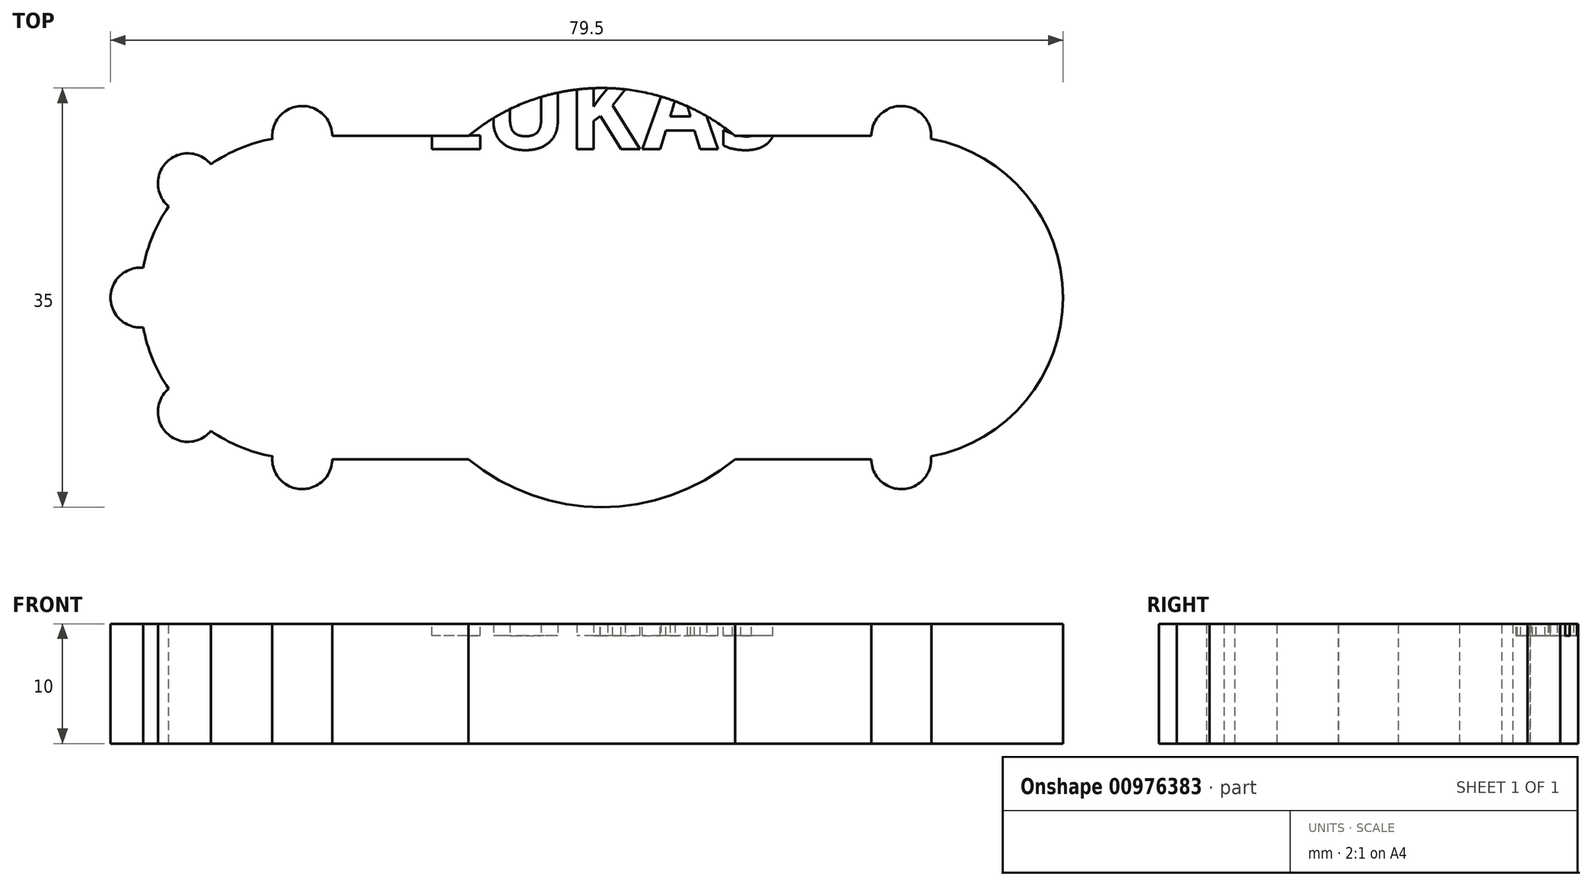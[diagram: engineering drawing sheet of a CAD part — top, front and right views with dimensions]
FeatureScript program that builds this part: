
annotation { "Feature Type Name" : "Feature", "Feature Type Description" : "" }
export const myFeature = defineFeature(function(context is Context, id is Id, definition is map)
    precondition{}
    {
        {
            var Q0;
            Q0=qCreatedBy(makeId("Top.planeOp"),FACE);
            var sketch = newSketch(context, id + "F0", { "sketchPlane" : qUnion([Q0])});
            skLineSegment(sketch, "E0.bottom", {"start": v(25, 13.5) * mm, "end": v(-25, 13.5) * mm});
            skLineSegment(sketch, "E0.top", {"start": v(25, -13.5) * mm, "end": v(-25, -13.5) * mm});
            skLineSegment(sketch, "E0.left", {"start": v(25, 13.5) * mm, "end": v(25, -13.5) * mm});
            skLineSegment(sketch, "E0.right", {"start": v(-25, 13.5) * mm, "end": v(-25, -13.5) * mm});
            skPoint(sketch, "E0.middle", {"position": v(0, 0) * mm});
            skCircle(sketch, "E1", {"center": v(-25, 0) * mm, "radius": 13.5 * mm});
            skCircle(sketch, "E2", {"center": v(25, 0) * mm, "radius": 13.5 * mm});
            skCircle(sketch, "E3", {"center": v(0, 0) * mm, "radius": 11.05 * mm});
            skCircle(sketch, "E4.cCircle", {"center": v(-25, 0) * mm, "radius": 8.55 * mm, "construction": true});
            skLineSegment(sketch, "E4.0", {"start": v(-25, 9.87) * mm, "end": v(-16.45, 4.94) * mm});
            skLineSegment(sketch, "E4.1", {"start": v(-16.45, 4.94) * mm, "end": v(-16.45, -4.94) * mm});
            skLineSegment(sketch, "E4.2", {"start": v(-16.45, -4.94) * mm, "end": v(-25, -9.87) * mm});
            skLineSegment(sketch, "E4.3", {"start": v(-25, -9.87) * mm, "end": v(-33.55, -4.94) * mm});
            skLineSegment(sketch, "E4.4", {"start": v(-33.55, -4.94) * mm, "end": v(-33.55, 4.94) * mm});
            skLineSegment(sketch, "E4.5", {"start": v(-33.55, 4.94) * mm, "end": v(-25, 9.87) * mm});
            skPoint(sketch, "E4.0.midPoint", {"position": v(-20.73, 7.4) * mm});
            skCircle(sketch, "E5.cCircle", {"center": v(25, 0) * mm, "radius": 8.55 * mm, "construction": true});
            skLineSegment(sketch, "E5.0", {"start": v(25, 9.87) * mm, "end": v(33.55, 4.94) * mm});
            skLineSegment(sketch, "E5.1", {"start": v(33.55, 4.94) * mm, "end": v(33.55, -4.94) * mm});
            skLineSegment(sketch, "E5.2", {"start": v(33.55, -4.94) * mm, "end": v(25, -9.87) * mm});
            skLineSegment(sketch, "E5.3", {"start": v(25, -9.87) * mm, "end": v(16.45, -4.94) * mm});
            skLineSegment(sketch, "E5.4", {"start": v(16.45, -4.94) * mm, "end": v(16.45, 4.94) * mm});
            skLineSegment(sketch, "E5.5", {"start": v(16.45, 4.94) * mm, "end": v(25, 9.87) * mm});
            skPoint(sketch, "E5.0.midPoint", {"position": v(29.27, 7.4) * mm});
            skArc(sketch, "E6", {"start": v(-14.98, 9.05) * mm, "mid": v(-17.5, 0) * mm, "end": v(-14.98, -9.05) * mm, "construction": true});
            skArc(sketch, "E7.trimOffspring", {"start": v(11.14, 13.5) * mm, "mid": v(0, 17.5) * mm, "end": v(-11.14, 13.5) * mm});
            skArc(sketch, "E8.trimOffspring", {"start": v(14.98, -9.05) * mm, "mid": v(17.5, 0) * mm, "end": v(14.98, 9.05) * mm, "construction": true});
            skArc(sketch, "E9.trimOffspring", {"start": v(-11.14, -13.5) * mm, "mid": v(0, -17.5) * mm, "end": v(11.14, -13.5) * mm});
            skSolve(sketch);
        }
        {
            var Q0;
            Q0 = qSketchRegion(id + "F0", true);
            extrude(context, id + "F1", {"entities" : qUnion([Q0]), "endBound" : BoundingType.SYMMETRIC, "depth" : 10 * mm, "offsetDistance" : 25.4 * mm});
        }
        {
            var Q0;
            Q0=qCreatedBy(makeId("Top.planeOp"),FACE);
            var sketch = newSketch(context, id + "F2", { "sketchPlane" : qUnion([Q0])});
            skArc(sketch, "E10.0", {"start": v(-25, 13.5) * mm, "mid": v(-38.5, 0) * mm, "end": v(-25, -13.5) * mm});
            skLineSegment(sketch, "E11.0", {"start": v(25, 13.5) * mm, "end": v(-25, 13.5) * mm});
            skArc(sketch, "E12.0", {"start": v(25, -13.5) * mm, "mid": v(38.5, 0) * mm, "end": v(25, 13.5) * mm});
            skLineSegment(sketch, "E13.0", {"start": v(25, -13.5) * mm, "end": v(-25, -13.5) * mm});
            skCircle(sketch, "E14", {"center": v(-25, 13.5) * mm, "radius": 2.5 * mm});
            skCircle(sketch, "E15.1.0", {"center": v(-34.55, 9.55) * mm, "radius": 2.5 * mm});
            skCircle(sketch, "E15.2.0", {"center": v(-38.5, 0) * mm, "radius": 2.5 * mm});
            skCircle(sketch, "E15.3.0", {"center": v(-34.55, -9.55) * mm, "radius": 2.5 * mm});
            skCircle(sketch, "E15.4.0", {"center": v(-25, -13.5) * mm, "radius": 2.5 * mm});
            skLineSegment(sketch, "E15.anchor1", {"start": v(-25, 0) * mm, "end": v(-25, 13.5) * mm, "construction": true});
            skLineSegment(sketch, "E15.anchor2", {"start": v(-25, 0) * mm, "end": v(-25, -13.5) * mm, "construction": true});
            skLineSegment(sketch, "E16.MirrorCS", {"start": v(25, 0) * mm, "end": v(25, -13.5) * mm, "construction": true});
            skLineSegment(sketch, "E17.MirrorCS", {"start": v(25, 0) * mm, "end": v(25, 13.5) * mm, "construction": true});
            skCircle(sketch, "E18.MirrorC", {"center": v(25, -13.5) * mm, "radius": 2.5 * mm});
            skCircle(sketch, "E19.MirrorC", {"center": v(34.55, -9.55) * mm, "radius": 2.5 * mm});
            skCircle(sketch, "E20.MirrorC", {"center": v(38.5, 0) * mm, "radius": 2.5 * mm});
            skArc(sketch, "E21.MirrorCS", {"start": v(25, 13.5) * mm, "mid": v(38.5, 0) * mm, "end": v(25, -13.5) * mm});
            skCircle(sketch, "E22.MirrorC", {"center": v(34.55, 9.55) * mm, "radius": 2.5 * mm});
            skCircle(sketch, "E23.MirrorC", {"center": v(25, 13.5) * mm, "radius": 2.5 * mm});
            skSolve(sketch);
        }
        {
            var Q0;
            {var subQ0=sQuery(id+"F2.wireOp",EDGE,"E11.0");var subQ1=sQuery(id+"F2.wireOp",EDGE,"E10.0");var subQ2=makeQuery(id+"F2.imprint","INTERSECT",VERTEX,{"derivedFrom":[subQ1,subQ0]});Q0=makeQuery(id+"F2.imprint","IMPRINT",FACE,{"disambiguationData":[TD([[makeQuery(id+"F2.imprint","IMPRINT",EDGE,{"disambiguationData":[TD([[subQ2,-1.0]])],"derivedFrom":subQ1}),-1.0]])]});}
            var Q1;
            {var subQ0=sQuery(id+"F2.wireOp",EDGE,"E15.1.0");var subQ1=sQuery(id+"F2.wireOp",EDGE,"E10.0");var subQ2=makeQuery(id+"F2.imprint","INTERSECT",VERTEX,{"disambiguationData":[OD(0.0)],"derivedFrom":[subQ1,subQ0]});Q1=makeQuery(id+"F2.imprint","IMPRINT",FACE,{"disambiguationData":[TD([[makeQuery(id+"F2.imprint","IMPRINT",EDGE,{"disambiguationData":[TD([[subQ2,-1.0]])],"derivedFrom":subQ1}),-1.0]])]});}
            var Q2;
            {var subQ0=sQuery(id+"F2.wireOp",EDGE,"E15.2.0");var subQ1=sQuery(id+"F2.wireOp",EDGE,"E10.0");var subQ2=makeQuery(id+"F2.imprint","INTERSECT",VERTEX,{"disambiguationData":[OD(0.0)],"derivedFrom":[subQ1,subQ0]});Q2=makeQuery(id+"F2.imprint","IMPRINT",FACE,{"disambiguationData":[TD([[makeQuery(id+"F2.imprint","IMPRINT",EDGE,{"disambiguationData":[TD([[subQ2,-1.0]])],"derivedFrom":subQ1}),-1.0]])]});}
            var Q3;
            {var subQ0=sQuery(id+"F2.wireOp",EDGE,"E15.3.0");var subQ1=sQuery(id+"F2.wireOp",EDGE,"E10.0");var subQ2=makeQuery(id+"F2.imprint","INTERSECT",VERTEX,{"disambiguationData":[OD(0.0)],"derivedFrom":[subQ1,subQ0]});Q3=makeQuery(id+"F2.imprint","IMPRINT",FACE,{"disambiguationData":[TD([[makeQuery(id+"F2.imprint","IMPRINT",EDGE,{"disambiguationData":[TD([[subQ2,-1.0]])],"derivedFrom":subQ1}),-1.0]])]});}
            var Q4;
            {var subQ0=sQuery(id+"F2.wireOp",EDGE,"E13.0");var subQ1=sQuery(id+"F2.wireOp",EDGE,"E10.0");var subQ2=makeQuery(id+"F2.imprint","INTERSECT",VERTEX,{"derivedFrom":[subQ1,subQ0]});Q4=makeQuery(id+"F2.imprint","IMPRINT",FACE,{"disambiguationData":[TD([[makeQuery(id+"F2.imprint","IMPRINT",EDGE,{"disambiguationData":[TD([[subQ2,1.0]])],"derivedFrom":subQ1}),-1.0]])]});}
            var Q5;
            {var subQ0=sQuery(id+"F2.wireOp",EDGE,"E21.MirrorCS");var subQ1=sQuery(id+"F2.wireOp",EDGE,"E11.0");var subQ2=makeQuery(id+"F2.imprint","INTERSECT",VERTEX,{"derivedFrom":[subQ1,subQ0]});Q5=makeQuery(id+"F2.imprint","IMPRINT",FACE,{"disambiguationData":[TD([[makeQuery(id+"F2.imprint","IMPRINT",EDGE,{"disambiguationData":[TD([[subQ2,-1.0]])],"derivedFrom":subQ1}),-1.0]])]});}
            var Q6;
            {var subQ0=sQuery(id+"F2.wireOp",EDGE,"E21.MirrorCS");var subQ1=sQuery(id+"F2.wireOp",EDGE,"E13.0");var subQ2=makeQuery(id+"F2.imprint","INTERSECT",VERTEX,{"derivedFrom":[subQ1,subQ0]});Q6=makeQuery(id+"F2.imprint","IMPRINT",FACE,{"disambiguationData":[TD([[makeQuery(id+"F2.imprint","IMPRINT",EDGE,{"disambiguationData":[TD([[subQ2,-1.0]])],"derivedFrom":subQ1}),1.0]])]});}
            var Q7;
            {var subQ0=sQuery(id+"F2.wireOp",EDGE,"E21.MirrorCS");var subQ1=sQuery(id+"F2.wireOp",EDGE,"E19.MirrorC");var subQ2=makeQuery(id+"F2.imprint","INTERSECT",VERTEX,{"disambiguationData":[OD(0.0)],"derivedFrom":[subQ1,subQ0]});Q7=makeQuery(id+"F2.imprint","IMPRINT",FACE,{"disambiguationData":[TD([[makeQuery(id+"F2.imprint","IMPRINT",EDGE,{"disambiguationData":[TD([[subQ2,-1.0]])],"derivedFrom":subQ1}),-1.0]])]});}
            var Q8;
            {var subQ0=sQuery(id+"F2.wireOp",EDGE,"E21.MirrorCS");var subQ1=sQuery(id+"F2.wireOp",EDGE,"E20.MirrorC");var subQ2=makeQuery(id+"F2.imprint","INTERSECT",VERTEX,{"disambiguationData":[OD(0.0)],"derivedFrom":[subQ1,subQ0]});Q8=makeQuery(id+"F2.imprint","IMPRINT",FACE,{"disambiguationData":[TD([[makeQuery(id+"F2.imprint","IMPRINT",EDGE,{"disambiguationData":[TD([[subQ2,-1.0]])],"derivedFrom":subQ1}),-1.0]])]});}
            var Q9;
            {var subQ0=sQuery(id+"F2.wireOp",EDGE,"E22.MirrorC");var subQ1=sQuery(id+"F2.wireOp",EDGE,"E21.MirrorCS");var subQ2=makeQuery(id+"F2.imprint","INTERSECT",VERTEX,{"disambiguationData":[OD(0.0)],"derivedFrom":[subQ1,subQ0]});Q9=makeQuery(id+"F2.imprint","IMPRINT",FACE,{"disambiguationData":[TD([[makeQuery(id+"F2.imprint","IMPRINT",EDGE,{"disambiguationData":[TD([[subQ2,-1.0]])],"derivedFrom":subQ1}),1.0]])]});}
            var Q10;
            {var subQ0=sQuery(id+"F2.wireOp",EDGE,"E11.0");var subQ1=sQuery(id+"F2.wireOp",EDGE,"E10.0");var subQ2=makeQuery(id+"F2.imprint","INTERSECT",VERTEX,{"derivedFrom":[subQ1,subQ0]});Q10=makeQuery(id+"F2.imprint","IMPRINT",FACE,{"disambiguationData":[TD([[makeQuery(id+"F2.imprint","IMPRINT",EDGE,{"disambiguationData":[TD([[subQ2,-1.0]])],"derivedFrom":subQ1}),1.0]])]});}
            var Q11;
            {var subQ0=sQuery(id+"F2.wireOp",EDGE,"E15.1.0");var subQ1=sQuery(id+"F2.wireOp",EDGE,"E10.0");var subQ2=makeQuery(id+"F2.imprint","INTERSECT",VERTEX,{"disambiguationData":[OD(0.0)],"derivedFrom":[subQ1,subQ0]});Q11=makeQuery(id+"F2.imprint","IMPRINT",FACE,{"disambiguationData":[TD([[makeQuery(id+"F2.imprint","IMPRINT",EDGE,{"disambiguationData":[TD([[subQ2,-1.0]])],"derivedFrom":subQ1}),1.0]])]});}
            var Q12;
            {var subQ0=sQuery(id+"F2.wireOp",EDGE,"E15.2.0");var subQ1=sQuery(id+"F2.wireOp",EDGE,"E10.0");var subQ2=makeQuery(id+"F2.imprint","INTERSECT",VERTEX,{"disambiguationData":[OD(0.0)],"derivedFrom":[subQ1,subQ0]});Q12=makeQuery(id+"F2.imprint","IMPRINT",FACE,{"disambiguationData":[TD([[makeQuery(id+"F2.imprint","IMPRINT",EDGE,{"disambiguationData":[TD([[subQ2,-1.0]])],"derivedFrom":subQ1}),1.0]])]});}
            var Q13;
            {var subQ0=sQuery(id+"F2.wireOp",EDGE,"E15.3.0");var subQ1=sQuery(id+"F2.wireOp",EDGE,"E10.0");var subQ2=makeQuery(id+"F2.imprint","INTERSECT",VERTEX,{"disambiguationData":[OD(0.0)],"derivedFrom":[subQ1,subQ0]});Q13=makeQuery(id+"F2.imprint","IMPRINT",FACE,{"disambiguationData":[TD([[makeQuery(id+"F2.imprint","IMPRINT",EDGE,{"disambiguationData":[TD([[subQ2,-1.0]])],"derivedFrom":subQ1}),1.0]])]});}
            var Q14;
            {var subQ0=sQuery(id+"F2.wireOp",EDGE,"E13.0");var subQ1=sQuery(id+"F2.wireOp",EDGE,"E10.0");var subQ2=makeQuery(id+"F2.imprint","INTERSECT",VERTEX,{"derivedFrom":[subQ1,subQ0]});Q14=makeQuery(id+"F2.imprint","IMPRINT",FACE,{"disambiguationData":[TD([[makeQuery(id+"F2.imprint","IMPRINT",EDGE,{"disambiguationData":[TD([[subQ2,1.0]])],"derivedFrom":subQ1}),1.0]])]});}
            var Q15;
            {var subQ0=sQuery(id+"F2.wireOp",EDGE,"E21.MirrorCS");var subQ1=sQuery(id+"F2.wireOp",EDGE,"E11.0");var subQ2=makeQuery(id+"F2.imprint","INTERSECT",VERTEX,{"derivedFrom":[subQ1,subQ0]});Q15=makeQuery(id+"F2.imprint","IMPRINT",FACE,{"disambiguationData":[TD([[makeQuery(id+"F2.imprint","IMPRINT",EDGE,{"disambiguationData":[TD([[subQ2,-1.0]])],"derivedFrom":subQ1}),1.0]])]});}
            var Q16;
            {var subQ0=sQuery(id+"F2.wireOp",EDGE,"E21.MirrorCS");var subQ1=sQuery(id+"F2.wireOp",EDGE,"E13.0");var subQ2=makeQuery(id+"F2.imprint","INTERSECT",VERTEX,{"derivedFrom":[subQ1,subQ0]});Q16=makeQuery(id+"F2.imprint","IMPRINT",FACE,{"disambiguationData":[TD([[makeQuery(id+"F2.imprint","IMPRINT",EDGE,{"disambiguationData":[TD([[subQ2,-1.0]])],"derivedFrom":subQ1}),-1.0]])]});}
            var Q17;
            {var subQ0=sQuery(id+"F2.wireOp",EDGE,"E21.MirrorCS");var subQ1=sQuery(id+"F2.wireOp",EDGE,"E19.MirrorC");var subQ2=makeQuery(id+"F2.imprint","INTERSECT",VERTEX,{"disambiguationData":[OD(0.0)],"derivedFrom":[subQ1,subQ0]});Q17=makeQuery(id+"F2.imprint","IMPRINT",FACE,{"disambiguationData":[TD([[makeQuery(id+"F2.imprint","IMPRINT",EDGE,{"disambiguationData":[TD([[subQ2,1.0]])],"derivedFrom":subQ1}),-1.0]])]});}
            var Q18;
            {var subQ0=sQuery(id+"F2.wireOp",EDGE,"E21.MirrorCS");var subQ1=sQuery(id+"F2.wireOp",EDGE,"E20.MirrorC");var subQ2=makeQuery(id+"F2.imprint","INTERSECT",VERTEX,{"disambiguationData":[OD(0.0)],"derivedFrom":[subQ1,subQ0]});Q18=makeQuery(id+"F2.imprint","IMPRINT",FACE,{"disambiguationData":[TD([[makeQuery(id+"F2.imprint","IMPRINT",EDGE,{"disambiguationData":[TD([[subQ2,1.0]])],"derivedFrom":subQ1}),-1.0]])]});}
            var Q19;
            {var subQ0=sQuery(id+"F2.wireOp",EDGE,"E22.MirrorC");var subQ1=sQuery(id+"F2.wireOp",EDGE,"E21.MirrorCS");var subQ2=makeQuery(id+"F2.imprint","INTERSECT",VERTEX,{"disambiguationData":[OD(0.0)],"derivedFrom":[subQ1,subQ0]});Q19=makeQuery(id+"F2.imprint","IMPRINT",FACE,{"disambiguationData":[TD([[makeQuery(id+"F2.imprint","IMPRINT",EDGE,{"disambiguationData":[TD([[subQ2,-1.0]])],"derivedFrom":subQ1}),-1.0]])]});}
            extrude(context, id + "F3", {"entities" : qUnion([Q0, Q1, Q2, Q3, Q4, Q5, Q6, Q7, Q8, Q9, Q10, Q11, Q12, Q13, Q14, Q15, Q16, Q17, Q18, Q19]), "operationType" : NewBodyOperationType.ADD, "endBound" : BoundingType.SYMMETRIC, "oppositeDirection" : true, "depth" : 10 * mm, "offsetDistance" : 25 * mm});
        }
        {
            var Q0;
            Q0=makeQuery(id+"F3.boolean.opBoolean","MERGE",FACE,{"derivedFrom":[makeQuery(id+"F1.opExtrude","CAP_FACE",FACE,{"disambiguationData":[OSD([sQuery(id+"F0.wireOp",EDGE,"E0.bottom"),sQuery(id+"F0.wireOp",EDGE,"E0.top"),sQuery(id+"F0.wireOp",EDGE,"E1"),sQuery(id+"F0.wireOp",EDGE,"E2"),sQuery(id+"F0.wireOp",EDGE,"E3"),sQuery(id+"F0.wireOp",EDGE,"E4.0"),sQuery(id+"F0.wireOp",EDGE,"E4.1"),sQuery(id+"F0.wireOp",EDGE,"E4.2"),sQuery(id+"F0.wireOp",EDGE,"E4.3"),sQuery(id+"F0.wireOp",EDGE,"E4.4"),sQuery(id+"F0.wireOp",EDGE,"E4.5"),sQuery(id+"F0.wireOp",EDGE,"E5.0"),sQuery(id+"F0.wireOp",EDGE,"E5.1"),sQuery(id+"F0.wireOp",EDGE,"E5.2"),sQuery(id+"F0.wireOp",EDGE,"E5.3"),sQuery(id+"F0.wireOp",EDGE,"E5.4"),sQuery(id+"F0.wireOp",EDGE,"E5.5")])],"isStart":false}),makeQuery(id+"F3.opExtrude","CAP_FACE",FACE,{"disambiguationData":[OSD([sQuery(id+"F2.wireOp",EDGE,"E14")])],"isStart":true}),makeQuery(id+"F3.opExtrude","CAP_FACE",FACE,{"disambiguationData":[OSD([sQuery(id+"F2.wireOp",EDGE,"E15.1.0")])],"isStart":true}),makeQuery(id+"F3.opExtrude","CAP_FACE",FACE,{"disambiguationData":[OSD([sQuery(id+"F2.wireOp",EDGE,"E15.2.0")])],"isStart":true}),makeQuery(id+"F3.opExtrude","CAP_FACE",FACE,{"disambiguationData":[OSD([sQuery(id+"F2.wireOp",EDGE,"E15.3.0")])],"isStart":true}),makeQuery(id+"F3.opExtrude","CAP_FACE",FACE,{"disambiguationData":[OSD([sQuery(id+"F2.wireOp",EDGE,"E15.4.0")])],"isStart":true}),makeQuery(id+"F3.opExtrude","CAP_FACE",FACE,{"disambiguationData":[OSD([sQuery(id+"F2.wireOp",EDGE,"E18.MirrorC")])],"isStart":true}),makeQuery(id+"F3.opExtrude","CAP_FACE",FACE,{"disambiguationData":[OSD([sQuery(id+"F2.wireOp",EDGE,"E19.MirrorC")])],"isStart":true}),makeQuery(id+"F3.opExtrude","CAP_FACE",FACE,{"disambiguationData":[OSD([sQuery(id+"F2.wireOp",EDGE,"E20.MirrorC")])],"isStart":true}),makeQuery(id+"F3.opExtrude","CAP_FACE",FACE,{"disambiguationData":[OSD([sQuery(id+"F2.wireOp",EDGE,"E22.MirrorC")])],"isStart":true}),makeQuery(id+"F3.opExtrude","CAP_FACE",FACE,{"disambiguationData":[OSD([sQuery(id+"F2.wireOp",EDGE,"E23.MirrorC")])],"isStart":true})]});
            var sketch = newSketch(context, id + "F4", { "sketchPlane" : qUnion([Q0])});
            skText(sketch, "E24", { "text": "LUKAS", "fontName": "OpenSans-Bold.ttf"});
            const initialGuessF4  = {"E24": [-0.015, 0.0124, 1, 0, 0.0066]};
            skSetInitialGuess(sketch, initialGuessF4);
            skSolve(sketch);
        }
        {
            var Q0;
            Q0 = qSketchRegion(id + "F4", true);
            extrude(context, id + "F5", {"entities" : qUnion([Q0]), "operationType" : NewBodyOperationType.REMOVE, "oppositeDirection" : true, "depth" : 1 * mm, "offsetDistance" : 25 * mm});
        }
    });
